# Revit family: Plymold-Essentials-Round_Tube-Table_Base-
name_source: partatom
category: Furniture
units: mm (PartAtom-declared; Revit-internal decimal feet)

## family parameters
Always vertical = Yes
Cut with Voids When Loaded = No
OmniClass Number = 23.40.20.00
OmniClass Title = General Furniture and Specialties
Render Appearance Source = Family Geometry
Room Calculation Point = No
Shared = No
Work Plane-Based = No

## types (4) — shared parameters
Assembly Code = E2020200
BASE MATERIAL = PLY - Onyx Black Powdercoat
Brand = Table Bases
CAP MATERIAL = PLY - Plastic Black
Default Elevation = 0"
GLIDES MATERIAL = PLY - Plastic Black
Height = 30"
Keynote = 12500
Manufacturer = Plymold
Product Documentation Link = https://plymold.com
Revit Model Built By = https://www.servex-us.com
Sustainability = https://plymold.com
Type Comments = Tables
URL = https://plymold.com
zero-valued in all types: Cost

## per-type parameters (varying)
| type | Depth | Description | Width |
| 1113022P | 22" | Round Tube Table Base Dining Height - 22"W x 22"D x 30”H | 22" |
| 1113030P | 30" | Round Tube Table Base Dining Height - 30"W x 30"D x 30”H | 30" |
| 1113036P | 36" | Round Tube Table Base Dining Height - 36"W x 36"D x 30”H | 36" |
| 11130226P | 26" | Round Tube Table Base Dining Height - 22"W x 26"D x 30”H | 22" |

note: column(s) folded — value = type name in every type: Model

## geometry (parser evidence)
native form markers: Sweep x4
no freeform markers — native parametric forms only
